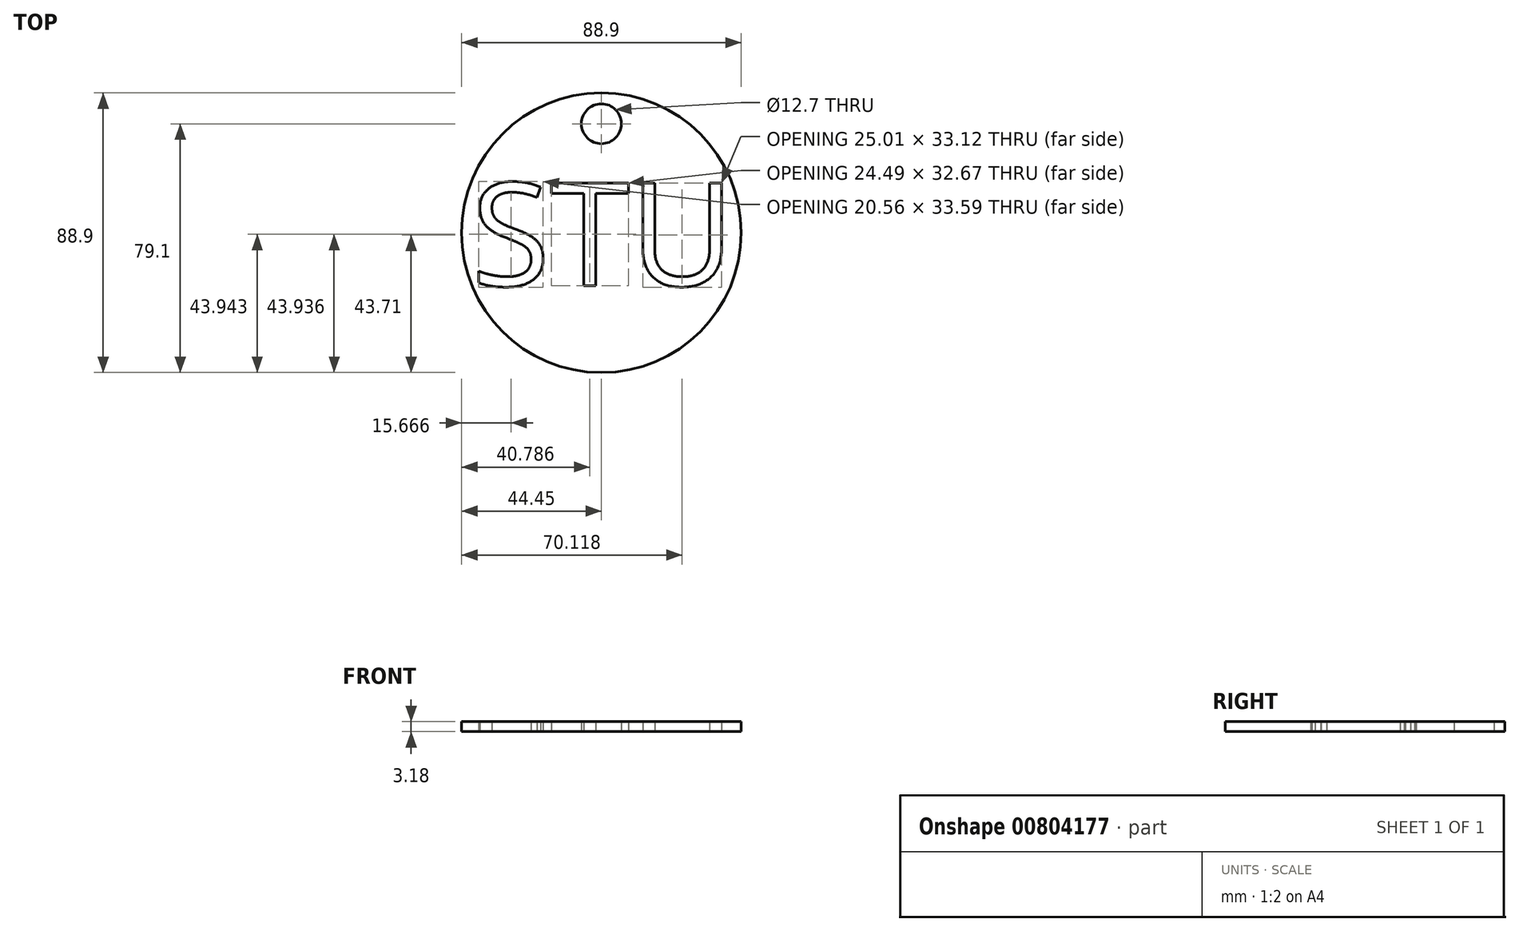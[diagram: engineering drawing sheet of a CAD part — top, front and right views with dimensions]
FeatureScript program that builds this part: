
annotation { "Feature Type Name" : "Feature", "Feature Type Description" : "" }
export const myFeature = defineFeature(function(context is Context, id is Id, definition is map)
    precondition{}
    {
        {
            var Q0;
            Q0=qCreatedBy(makeId("Top.planeOp"),FACE);
            var sketch = newSketch(context, id + "F0", { "sketchPlane" : qUnion([Q0])});
            skCircle(sketch, "E0", {"center": v(0, 0) * mm, "radius": 44.45 * mm});
            skCircle(sketch, "E1", {"center": v(0, 34.65) * mm, "radius": 6.35 * mm});
            skText(sketch, "E2", { "text": "STU", "fontName": "OpenSans-Regular.ttf"});
            const initialGuessF0  = {"E2": [-0.04143, -0.01685, 1, 0, 0.03295]};
            skSetInitialGuess(sketch, initialGuessF0);
            skSolve(sketch);
        }
        {
            var Q0;
            Q0=makeQuery(id+"F0.imprint","IMPRINT",FACE,{"disambiguationData":[TD([[makeQuery(id+"F0.imprint","IMPRINT",EDGE,{"derivedFrom":sQuery(id+"F0.wireOp",EDGE,"E0")}),1.0]])]});
            extrude(context, id + "F1", {"entities" : qUnion([Q0]), "depth" : 3.17 * mm, "offsetDistance" : 25.4 * mm});
        }
    });
